# Revit family: Pump-Dual-Rheem-Redi-Set
name_source: partatom
category: Mechanical Equipment
revit_build: Autodesk Revit 2018 (Build: 20170927_1515(x64)
units: mm (PartAtom-declared; Revit-internal decimal feet)

## family parameters
Always vertical = Yes
Cut with Voids When Loaded = No
Host = Wall
OmniClass Number = 23.65.55.11
OmniClass Title = Supply Pumps and Compressors
Part Type = Normal
Room Calculation Point = No
Round Connector Dimension = Use Diameter
Shared = No

## types (1)
- This family uses a Type Catalogue
    AmbientTemperatureMax = 40 °C
    BaseFrameMaterial = Steel, Galvanized
    BottomPipeExtrusion = 81 mm
    ClampSize = 30 mm  [stored 0.0984252 ft]
    ControlPanelDepth = 145 mm  [stored 0.475722 ft]
    ControlPanelHeight = 300 mm
    ControlPanelWidth = 300 mm
    Default Elevation = 600 mm
    Description = Redi-set dual pump sets provide redundancy back up and are an ideal means of reducing energy consumption by timing the operation of the pumps when required. The systems incorporate Grundfos UPS 20-60N or UPS 32-80N stainless steel pump and brass manifolds. The complete system is mounted on a galvanized base frame with two holes on each side for easy mounting. The system includes non return valves and shut off valves integrated into a manifold arrangement to allow removal of one pump whilst the other is in operation.
    Diameter_ANZRS = 20 mm  [stored 0.0656168 ft]
    DischargePipeInset = 30 mm  [stored 0.0984252 ft]
    DischargePipeOffsetH = 81 mm
    FluidTemperatureMax = 110 °C
    FluidTemperatureMin = 2 °C
    Frequency_ANZRS = 50 Hz
    Height_ANZRS = 990 mm
    ImpellerBladeMaterial = Composite, PES/PP
    Light = No
    LightMaterial = Glass, Red
    Manufacturer = Rheem
    Material_ANZRS = Stainless Steel, Polished
    Model = Deluxe–UPS 20-60N
    ModifiedIssue_ANZRS = 20180310 $
    MotorDepth = 160 mm
    MotorMaterial = Composite, PES/PP
    MotorRadius = 50 mm  [stored 0.164042 ft]
    MountingHoleRadius = 5 mm  [stored 0.0164042 ft]
    NumberOfPhases_ANZRS = 1
    OperatingPressureMax = 1000.0 kPa
    PipeMaterial = Stainless Steel, Polished
    PipeOffset = 85 mm
    PipeRadius = 10 mm  [stored 0.0328084 ft]
    PipeSpacingH = 150 mm  [stored 0.492126 ft]
    ProductCode_ANZRS = 890666
    PumpCasingMaterial = Stainless Steel
    SuctionDischargeSpacingV = 451 mm  [stored 1.47966 ft]
    SuctionPipeHeightActual = 710 mm
    SuctionPipeInset = 20 mm  [stored 0.0656168 ft]
    SuctionPipeOffsetH = 91 mm
    SuctionPipeOffsetV = 100 mm  [stored 0.328084 ft]
    TopPipeExtrusion = 71 mm
    URL = http://www.rheem.com.au
    Voltage_ANZRS = 240 V
    Wattage_ANZRS = 0 W
    WeightNet_ANZRS = 23.70 kg
    Width_ANZRS = 340 mm

note: [stored X ft] marks values corroborated as IEEE doubles in the binary element streams (Revit-internal decimal feet)

## geometry (parser evidence)
native form markers: Extrusion x2, Sweep x4
no freeform markers — native parametric forms only
